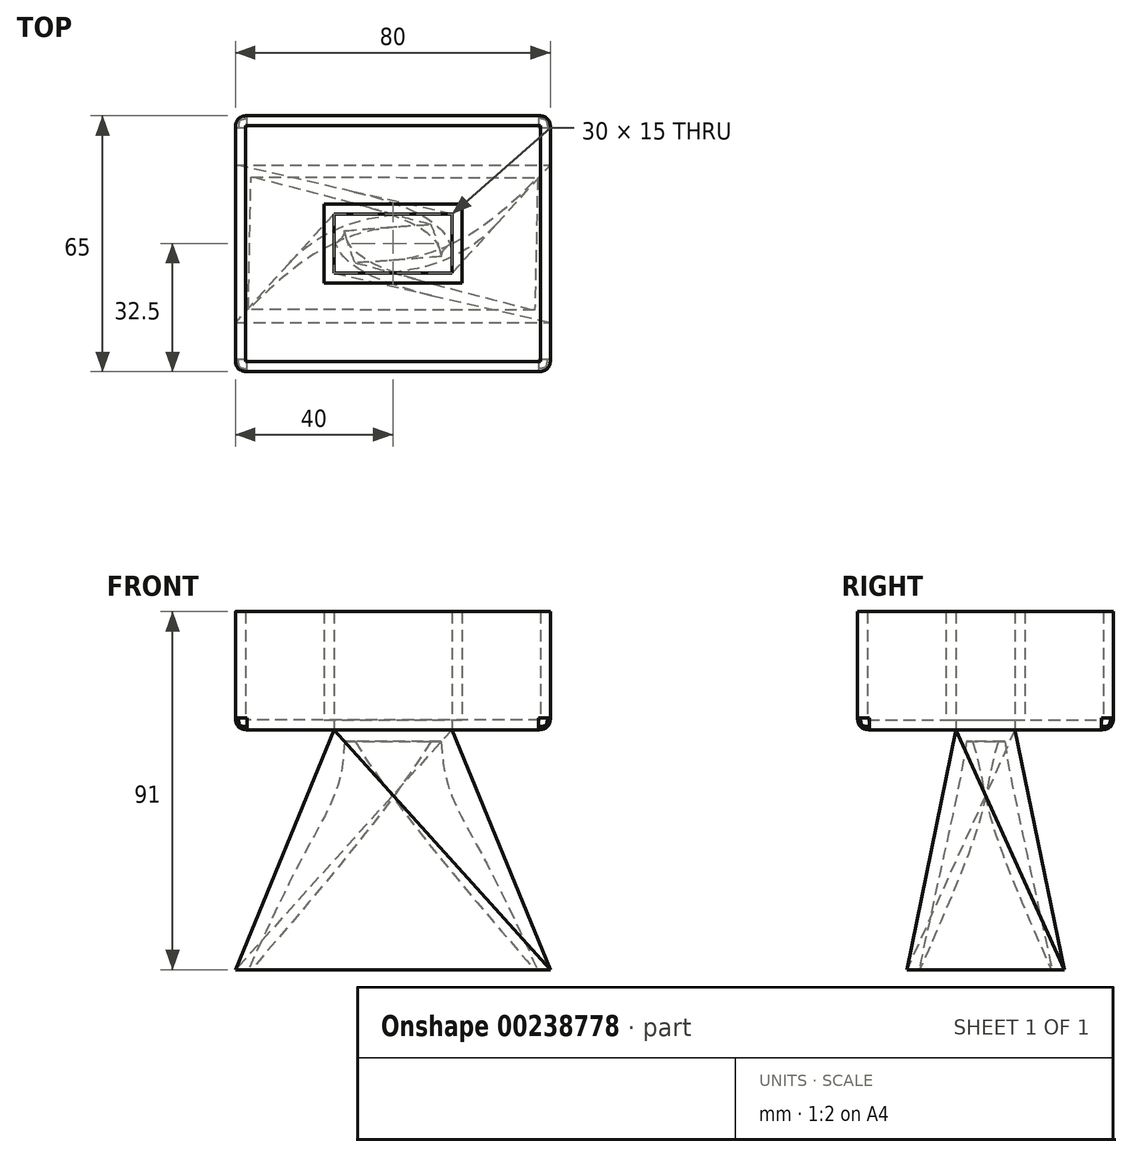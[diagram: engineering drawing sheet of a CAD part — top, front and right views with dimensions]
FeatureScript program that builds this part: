
annotation { "Feature Type Name" : "Feature", "Feature Type Description" : "" }
export const myFeature = defineFeature(function(context is Context, id is Id, definition is map)
    precondition{}
    {
        {
            var Q0;
            Q0=qCreatedBy(makeId("Top.planeOp"),FACE);
            var sketch = newSketch(context, id + "F0", { "sketchPlane" : qUnion([Q0])});
            skLineSegment(sketch, "E0.bottom", {"start": v(-40, 20) * mm, "end": v(40, 20) * mm});
            skLineSegment(sketch, "E0.top", {"start": v(-40, -20) * mm, "end": v(40, -20) * mm});
            skLineSegment(sketch, "E0.left", {"start": v(-40, 20) * mm, "end": v(-40, -20) * mm});
            skLineSegment(sketch, "E0.right", {"start": v(40, 20) * mm, "end": v(40, -20) * mm});
            skPoint(sketch, "E0.middle", {"position": v(0, 0) * mm});
            skSolve(sketch);
        }
        {
            var Q0;
            Q0=makeQuery(id+"F0.imprint","IMPRINT",FACE,{"disambiguationData":[TD([[makeQuery(id+"F0.imprint","IMPRINT",EDGE,{"derivedFrom":sQuery(id+"F0.wireOp",EDGE,"E0.bottom")}),-1.0]])]});
            cPlane(context, id + "F1", {"entities" : qUnion([Q0]), "cplaneType" : CPlaneType.OFFSET, "offset" : 61 * mm, "width" : 150 * mm, "height" : 150 * mm});
        }
        {
            var Q0;
            Q0=qCreatedBy(id+"F1.planeOp",FACE);
            var sketch = newSketch(context, id + "F2", { "sketchPlane" : qUnion([Q0])});
            skLineSegment(sketch, "E1.bottom", {"start": v(-15, 7.5) * mm, "end": v(15, 7.5) * mm});
            skLineSegment(sketch, "E1.top", {"start": v(-15, -7.5) * mm, "end": v(15, -7.5) * mm});
            skLineSegment(sketch, "E1.left", {"start": v(-15, 7.5) * mm, "end": v(-15, -7.5) * mm});
            skLineSegment(sketch, "E1.right", {"start": v(15, 7.5) * mm, "end": v(15, -7.5) * mm});
            skPoint(sketch, "E2", {"position": v(0, 0) * mm});
            skLineSegment(sketch, "E3", {"start": v(0, -22.4) * mm, "end": v(0, 20.1) * mm, "construction": true});
            skSolve(sketch);
        }
        {
            var Q0;
            Q0=makeQuery(id+"F2.imprint","IMPRINT",FACE,{"disambiguationData":[TD([[makeQuery(id+"F2.imprint","IMPRINT",EDGE,{"derivedFrom":sQuery(id+"F2.wireOp",EDGE,"E1.bottom")}),-1.0]])]});
            var Q1;
            Q1=makeQuery(id+"F0.imprint","IMPRINT",FACE,{"disambiguationData":[TD([[makeQuery(id+"F0.imprint","IMPRINT",EDGE,{"derivedFrom":sQuery(id+"F0.wireOp",EDGE,"E0.bottom")}),-1.0]])]});
            var Q2;
            Q2=sQuery(id+"F0.wireOp",VERTEX,"E0.right.end");
            var Q3;
            Q3=sQuery(id+"F2.wireOp",VERTEX,"E1.left.end");
            loft(context, id + "F3", {"sheetProfilesArray" : [{ "sheetProfileEntities" : qUnion([Q0]) }, { "sheetProfileEntities" : qUnion([Q1]) }], "matchConnections" : true, "connections" : [{ "connectionEntities" : qUnion([Q2, Q3]), "connectionEdgeQueries" : qUnion([]), "connectionEdgeParameters" : [] }]});
        }
        {
            var Q0;
            Q0=makeQuery(id+"F3.opLoft","CAP_FACE",FACE,{"disambiguationData":[OSD([makeQuery(id+"F0.imprint","IMPRINT",FACE,{"disambiguationData":[TD([[makeQuery(id+"F0.imprint","IMPRINT",EDGE,{"derivedFrom":sQuery(id+"F0.wireOp",EDGE,"E0.bottom")}),-1.0]])]})])],"isStart":true});
            shell(context, id + "F4", {"entities" : qUnion([Q0]), "thickness" : 3 * mm});
        }
        {
            var Q0;
            Q0=makeQuery(id+"F3.opLoft","CAP_FACE",FACE,{"disambiguationData":[OSD([makeQuery(id+"F2.imprint","IMPRINT",FACE,{"disambiguationData":[TD([[makeQuery(id+"F2.imprint","IMPRINT",EDGE,{"derivedFrom":sQuery(id+"F2.wireOp",EDGE,"E1.bottom")}),-1.0]])]})])],"isStart":true});
            var sketch = newSketch(context, id + "F5", { "sketchPlane" : qUnion([Q0])});
            skLineSegment(sketch, "E4.0", {"start": v(-40, -32.5) * mm, "end": v(-40, 32.5) * mm});
            skLineSegment(sketch, "E4.1", {"start": v(40, -32.5) * mm, "end": v(-40, -32.5) * mm});
            skLineSegment(sketch, "E4.2", {"start": v(40, -32.5) * mm, "end": v(40, 32.5) * mm});
            skLineSegment(sketch, "E4.3", {"start": v(40, 32.5) * mm, "end": v(-40, 32.5) * mm});
            skSolve(sketch);
        }
        {
            var Q0;
            Q0=makeQuery(id+"F5.imprint","IMPRINT",FACE,{"disambiguationData":[TD([[makeQuery(id+"F5.imprint","IMPRINT",EDGE,{"derivedFrom":sQuery(id+"F5.wireOp",EDGE,"E4.0")}),-1.0]])]});
            extrude(context, id + "F6", {"entities" : qUnion([Q0]), "depth" : 30 * mm});
        }
        {
            var Q0;
            Q0=makeQuery(id+"F6.opExtrude","CAP_FACE",FACE,{"disambiguationData":[OSD([sQuery(id+"F2.wireOp",EDGE,"E1.bottom"),sQuery(id+"F2.wireOp",EDGE,"E1.top"),sQuery(id+"F2.wireOp",EDGE,"E1.left"),sQuery(id+"F2.wireOp",EDGE,"E1.right"),sQuery(id+"F5.wireOp",EDGE,"E4.0"),sQuery(id+"F5.wireOp",EDGE,"E4.1"),sQuery(id+"F5.wireOp",EDGE,"E4.2"),sQuery(id+"F5.wireOp",EDGE,"E4.3")])],"isStart":false});
            shell(context, id + "F7", {"entities" : qUnion([Q0]), "thickness" : 2.5 * mm});
        }
        {
            var Q0;
            Q0=makeQuery(id+"F6.opExtrude","CAP_EDGE",EDGE,{"disambiguationData":[OSD([sQuery(id+"F5.wireOp",EDGE,"E4.2")])],"isStart":true});
            var Q1;
            Q1=makeQuery(id+"F6.opExtrude","CAP_EDGE",EDGE,{"disambiguationData":[OSD([sQuery(id+"F5.wireOp",EDGE,"E4.1")])],"isStart":true});
            var Q2;
            Q2=makeQuery(id+"F6.opExtrude","CAP_EDGE",EDGE,{"disambiguationData":[OSD([sQuery(id+"F5.wireOp",EDGE,"E4.3")])],"isStart":true});
            var Q3;
            Q3=makeQuery(id+"F6.opExtrude","CAP_EDGE",EDGE,{"disambiguationData":[OSD([sQuery(id+"F5.wireOp",EDGE,"E4.0")])],"isStart":true});
            var Q4;
            Q4=makeQuery(id+"F6.opExtrude","SWEPT_EDGE",EDGE,{"disambiguationData":[OSD([sQuery(id+"F5.wireOp",EDGE,"E4.0"),sQuery(id+"F5.wireOp",EDGE,"E4.3")])]});
            var Q5;
            Q5=makeQuery(id+"F6.opExtrude","SWEPT_EDGE",EDGE,{"disambiguationData":[OSD([sQuery(id+"F5.wireOp",EDGE,"E4.2"),sQuery(id+"F5.wireOp",EDGE,"E4.3")])]});
            var Q6;
            Q6=makeQuery(id+"F6.opExtrude","SWEPT_EDGE",EDGE,{"disambiguationData":[OSD([sQuery(id+"F5.wireOp",EDGE,"E4.1"),sQuery(id+"F5.wireOp",EDGE,"E4.2")])]});
            var Q7;
            Q7=makeQuery(id+"F6.opExtrude","SWEPT_EDGE",EDGE,{"disambiguationData":[OSD([sQuery(id+"F5.wireOp",EDGE,"E4.0"),sQuery(id+"F5.wireOp",EDGE,"E4.1")])]});
            fillet(context, id + "F8", {"entities" : qUnion([Q0, Q1, Q2, Q3, Q4, Q5, Q6, Q7]), "radius" : 3 * mm, "tangentPropagation" : true, "rho" : 0.5, "crossSection" : FilletCrossSection.CONIC, "allowEdgeOverflow" : false});
        }
    });
